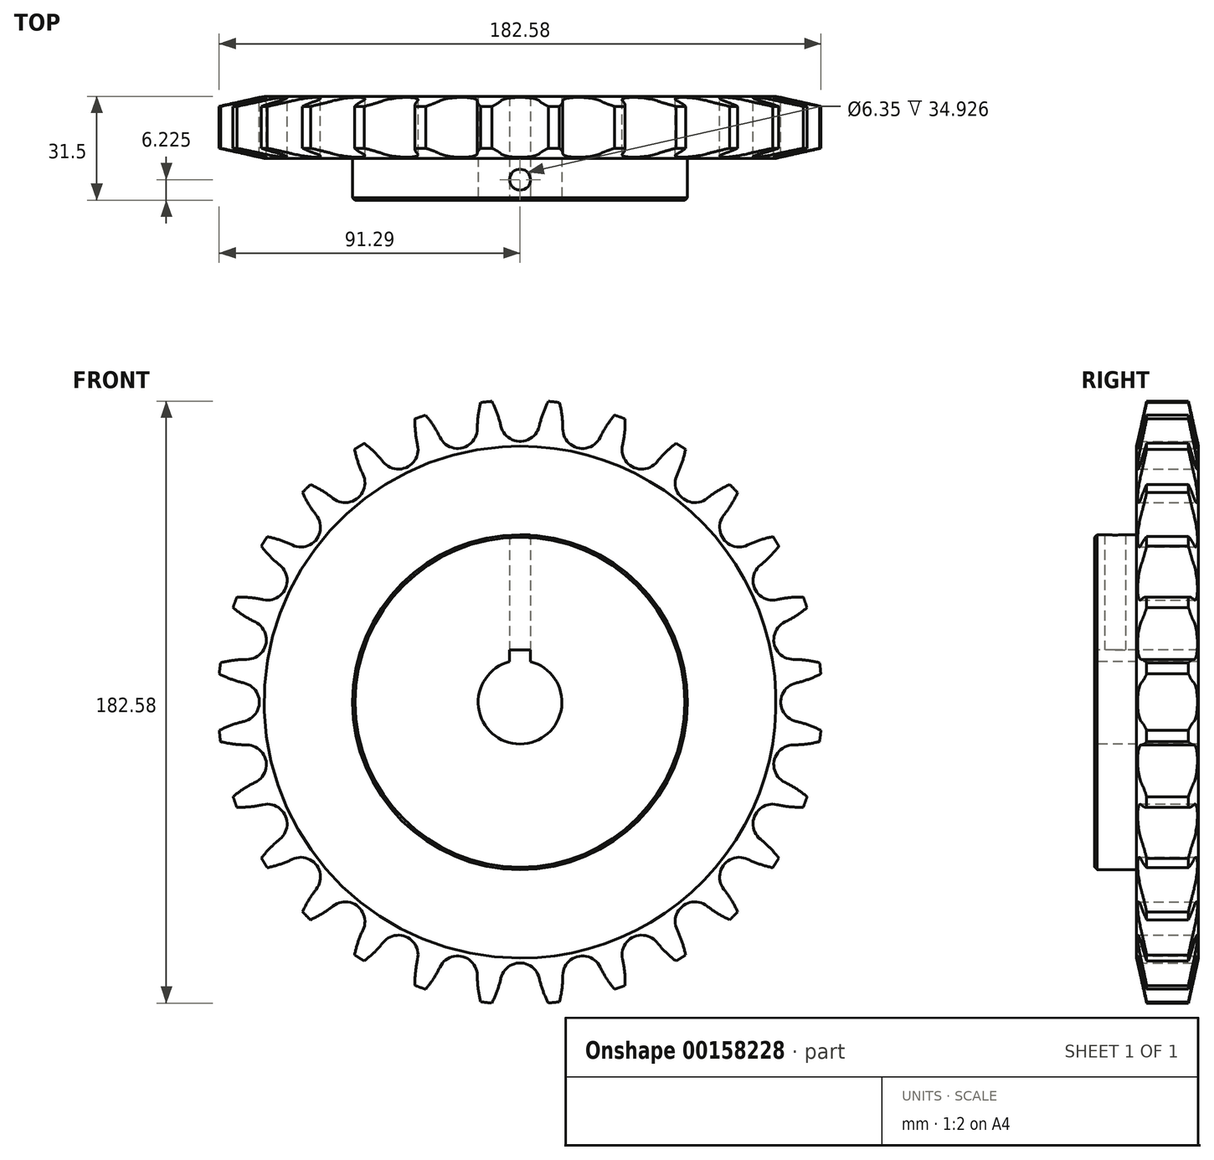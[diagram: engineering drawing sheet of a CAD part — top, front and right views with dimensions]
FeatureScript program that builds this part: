
annotation { "Feature Type Name" : "Feature", "Feature Type Description" : "" }
export const myFeature = defineFeature(function(context is Context, id is Id, definition is map)
    precondition{}
    {
        {
            var Q0;
            Q0=qCreatedBy(makeId("Front.planeOp"),FACE);
            var sketch = newSketch(context, id + "F0", { "sketchPlane" : qUnion([Q0])});
            skCircle(sketch, "E0", {"center": v(0, 0) * mm, "radius": 85.08 * mm, "construction": true});
            skArc(sketch, "E1", {"start": v(11.96, 90.87) * mm, "mid": v(10.27, 91.1) * mm, "end": v(8.58, 91.29) * mm});
            skArc(sketch, "E2", {"start": v(0, 79.1) * mm, "mid": v(3.72, 80.41) * mm, "end": v(5.82, 83.75) * mm});
            skArc(sketch, "E3", {"start": v(12.96, 82.94) * mm, "mid": v(14.26, 79.22) * mm, "end": v(17.6, 77.12) * mm});
            skArc(sketch, "E4", {"start": v(8.58, 91.29) * mm, "mid": v(6.96, 87.6) * mm, "end": v(5.82, 83.75) * mm});
            skArc(sketch, "E5.trimOffspring", {"start": v(12.96, 82.94) * mm, "mid": v(12.71, 86.94) * mm, "end": v(11.96, 90.87) * mm});
            skPoint(sketch, "E6.orphan", {"position": v(0, 104.4) * mm});
            skPoint(sketch, "E7.orphan", {"position": v(23.23, 101.77) * mm});
            skArc(sketch, "E8.1.1", {"start": v(-17.6, 77.12) * mm, "mid": v(-14.26, 79.22) * mm, "end": v(-12.96, 82.94) * mm});
            skArc(sketch, "E8.1.2", {"start": v(-11.95, 90.9) * mm, "mid": v(-12.7, 86.96) * mm, "end": v(-12.96, 82.94) * mm});
            skArc(sketch, "E8.1.3", {"start": v(-8.56, 91.26) * mm, "mid": v(-10.26, 91.1) * mm, "end": v(-11.95, 90.9) * mm});
            skArc(sketch, "E8.1.4", {"start": v(-5.82, 83.75) * mm, "mid": v(-6.95, 87.59) * mm, "end": v(-8.56, 91.26) * mm});
            skArc(sketch, "E8.1.5", {"start": v(-5.82, 83.75) * mm, "mid": v(-3.72, 80.41) * mm, "end": v(0, 79.1) * mm});
            skArc(sketch, "E8.2.1", {"start": v(-34.32, 71.27) * mm, "mid": v(-31.54, 74.06) * mm, "end": v(-31.1, 77.98) * mm});
            skArc(sketch, "E8.2.2", {"start": v(-31.88, 85.97) * mm, "mid": v(-31.74, 81.95) * mm, "end": v(-31.1, 77.98) * mm});
            skArc(sketch, "E8.2.3", {"start": v(-28.65, 87.06) * mm, "mid": v(-30.27, 86.53) * mm, "end": v(-31.88, 85.97) * mm});
            skArc(sketch, "E8.2.4", {"start": v(-24.3, 80.35) * mm, "mid": v(-26.27, 83.84) * mm, "end": v(-28.65, 87.06) * mm});
            skArc(sketch, "E8.2.5", {"start": v(-24.3, 80.35) * mm, "mid": v(-21.52, 77.57) * mm, "end": v(-17.6, 77.12) * mm});
            skArc(sketch, "E8.3.1", {"start": v(-49.32, 61.85) * mm, "mid": v(-47.23, 65.19) * mm, "end": v(-47.67, 69.1) * mm});
            skArc(sketch, "E8.3.2", {"start": v(-50.21, 76.72) * mm, "mid": v(-49.18, 72.83) * mm, "end": v(-47.67, 69.1) * mm});
            skArc(sketch, "E8.3.3", {"start": v(-47.3, 78.5) * mm, "mid": v(-48.77, 77.62) * mm, "end": v(-50.21, 76.72) * mm});
            skArc(sketch, "E8.3.4", {"start": v(-41.58, 72.93) * mm, "mid": v(-44.27, 75.9) * mm, "end": v(-47.3, 78.5) * mm});
            skArc(sketch, "E8.3.5", {"start": v(-41.58, 72.93) * mm, "mid": v(-38.24, 70.83) * mm, "end": v(-34.32, 71.27) * mm});
            skArc(sketch, "E8.4.1", {"start": v(-61.85, 49.32) * mm, "mid": v(-60.55, 53.04) * mm, "end": v(-61.85, 56.77) * mm});
            skArc(sketch, "E8.4.2", {"start": v(-66.02, 63.62) * mm, "mid": v(-64.15, 60.06) * mm, "end": v(-61.85, 56.77) * mm});
            skArc(sketch, "E8.4.3", {"start": v(-63.59, 66) * mm, "mid": v(-64.82, 64.83) * mm, "end": v(-66.02, 63.62) * mm});
            skArc(sketch, "E8.4.4", {"start": v(-56.77, 61.85) * mm, "mid": v(-60.05, 64.14) * mm, "end": v(-63.59, 66) * mm});
            skArc(sketch, "E8.4.5", {"start": v(-56.77, 61.85) * mm, "mid": v(-53.04, 60.55) * mm, "end": v(-49.32, 61.85) * mm});
            skArc(sketch, "E8.5.1", {"start": v(-71.27, 34.32) * mm, "mid": v(-70.83, 38.24) * mm, "end": v(-72.93, 41.58) * mm});
            skArc(sketch, "E8.5.2", {"start": v(-78.53, 47.33) * mm, "mid": v(-75.9, 44.28) * mm, "end": v(-72.93, 41.58) * mm});
            skArc(sketch, "E8.5.3", {"start": v(-76.68, 50.2) * mm, "mid": v(-77.62, 48.78) * mm, "end": v(-78.53, 47.33) * mm});
            skArc(sketch, "E8.5.4", {"start": v(-69.1, 47.67) * mm, "mid": v(-72.81, 49.17) * mm, "end": v(-76.68, 50.2) * mm});
            skArc(sketch, "E8.5.5", {"start": v(-69.1, 47.67) * mm, "mid": v(-65.19, 47.23) * mm, "end": v(-61.85, 49.32) * mm});
            skArc(sketch, "E8.6.1", {"start": v(-77.12, 17.6) * mm, "mid": v(-77.57, 21.52) * mm, "end": v(-80.35, 24.3) * mm});
            skArc(sketch, "E8.6.2", {"start": v(-87.09, 28.67) * mm, "mid": v(-83.86, 26.28) * mm, "end": v(-80.35, 24.3) * mm});
            skArc(sketch, "E8.6.3", {"start": v(-85.93, 31.88) * mm, "mid": v(-86.53, 30.28) * mm, "end": v(-87.09, 28.67) * mm});
            skArc(sketch, "E8.6.4", {"start": v(-77.98, 31.1) * mm, "mid": v(-81.93, 31.74) * mm, "end": v(-85.93, 31.88) * mm});
            skArc(sketch, "E8.6.5", {"start": v(-77.98, 31.1) * mm, "mid": v(-74.06, 31.54) * mm, "end": v(-71.27, 34.32) * mm});
            skArc(sketch, "E8.7.1", {"start": v(-79.1, 0) * mm, "mid": v(-80.41, 3.72) * mm, "end": v(-83.75, 5.82) * mm});
            skArc(sketch, "E8.7.2", {"start": v(-91.29, 8.58) * mm, "mid": v(-87.6, 6.96) * mm, "end": v(-83.75, 5.82) * mm});
            skArc(sketch, "E8.7.3", {"start": v(-90.87, 11.96) * mm, "mid": v(-91.1, 10.27) * mm, "end": v(-91.29, 8.58) * mm});
            skArc(sketch, "E8.7.4", {"start": v(-82.94, 12.96) * mm, "mid": v(-86.94, 12.71) * mm, "end": v(-90.87, 11.96) * mm});
            skArc(sketch, "E8.7.5", {"start": v(-82.94, 12.96) * mm, "mid": v(-79.22, 14.26) * mm, "end": v(-77.12, 17.6) * mm});
            skArc(sketch, "E8.8.1", {"start": v(-77.12, -17.6) * mm, "mid": v(-79.22, -14.26) * mm, "end": v(-82.94, -12.96) * mm});
            skArc(sketch, "E8.8.2", {"start": v(-90.9, -11.95) * mm, "mid": v(-86.96, -12.7) * mm, "end": v(-82.94, -12.96) * mm});
            skArc(sketch, "E8.8.3", {"start": v(-91.26, -8.56) * mm, "mid": v(-91.1, -10.26) * mm, "end": v(-90.9, -11.95) * mm});
            skArc(sketch, "E8.8.4", {"start": v(-83.75, -5.82) * mm, "mid": v(-87.59, -6.95) * mm, "end": v(-91.26, -8.56) * mm});
            skArc(sketch, "E8.8.5", {"start": v(-83.75, -5.82) * mm, "mid": v(-80.41, -3.72) * mm, "end": v(-79.1, 0) * mm});
            skArc(sketch, "E8.9.1", {"start": v(-71.27, -34.32) * mm, "mid": v(-74.06, -31.54) * mm, "end": v(-77.98, -31.1) * mm});
            skArc(sketch, "E8.9.2", {"start": v(-85.97, -31.88) * mm, "mid": v(-81.95, -31.74) * mm, "end": v(-77.98, -31.1) * mm});
            skArc(sketch, "E8.9.3", {"start": v(-87.06, -28.65) * mm, "mid": v(-86.53, -30.27) * mm, "end": v(-85.97, -31.88) * mm});
            skArc(sketch, "E8.9.4", {"start": v(-80.35, -24.3) * mm, "mid": v(-83.84, -26.27) * mm, "end": v(-87.06, -28.65) * mm});
            skArc(sketch, "E8.9.5", {"start": v(-80.35, -24.3) * mm, "mid": v(-77.57, -21.52) * mm, "end": v(-77.12, -17.6) * mm});
            skArc(sketch, "E8.10.1", {"start": v(-61.85, -49.32) * mm, "mid": v(-65.19, -47.23) * mm, "end": v(-69.1, -47.67) * mm});
            skArc(sketch, "E8.10.2", {"start": v(-76.72, -50.21) * mm, "mid": v(-72.83, -49.18) * mm, "end": v(-69.1, -47.67) * mm});
            skArc(sketch, "E8.10.3", {"start": v(-78.5, -47.3) * mm, "mid": v(-77.62, -48.77) * mm, "end": v(-76.72, -50.21) * mm});
            skArc(sketch, "E8.10.4", {"start": v(-72.93, -41.58) * mm, "mid": v(-75.9, -44.27) * mm, "end": v(-78.5, -47.3) * mm});
            skArc(sketch, "E8.10.5", {"start": v(-72.93, -41.58) * mm, "mid": v(-70.83, -38.24) * mm, "end": v(-71.27, -34.32) * mm});
            skArc(sketch, "E8.11.1", {"start": v(-49.32, -61.85) * mm, "mid": v(-53.04, -60.55) * mm, "end": v(-56.77, -61.85) * mm});
            skArc(sketch, "E8.11.2", {"start": v(-63.62, -66.02) * mm, "mid": v(-60.06, -64.15) * mm, "end": v(-56.77, -61.85) * mm});
            skArc(sketch, "E8.11.3", {"start": v(-66, -63.59) * mm, "mid": v(-64.83, -64.82) * mm, "end": v(-63.62, -66.02) * mm});
            skArc(sketch, "E8.11.4", {"start": v(-61.85, -56.77) * mm, "mid": v(-64.14, -60.05) * mm, "end": v(-66, -63.59) * mm});
            skArc(sketch, "E8.11.5", {"start": v(-61.85, -56.77) * mm, "mid": v(-60.55, -53.04) * mm, "end": v(-61.85, -49.32) * mm});
            skArc(sketch, "E8.12.1", {"start": v(-34.32, -71.27) * mm, "mid": v(-38.24, -70.83) * mm, "end": v(-41.58, -72.93) * mm});
            skArc(sketch, "E8.12.2", {"start": v(-47.33, -78.53) * mm, "mid": v(-44.28, -75.9) * mm, "end": v(-41.58, -72.93) * mm});
            skArc(sketch, "E8.12.3", {"start": v(-50.2, -76.68) * mm, "mid": v(-48.78, -77.62) * mm, "end": v(-47.33, -78.53) * mm});
            skArc(sketch, "E8.12.4", {"start": v(-47.67, -69.1) * mm, "mid": v(-49.17, -72.81) * mm, "end": v(-50.2, -76.68) * mm});
            skArc(sketch, "E8.12.5", {"start": v(-47.67, -69.1) * mm, "mid": v(-47.23, -65.19) * mm, "end": v(-49.32, -61.85) * mm});
            skArc(sketch, "E8.13.1", {"start": v(-17.6, -77.12) * mm, "mid": v(-21.52, -77.57) * mm, "end": v(-24.3, -80.35) * mm});
            skArc(sketch, "E8.13.2", {"start": v(-28.67, -87.09) * mm, "mid": v(-26.28, -83.86) * mm, "end": v(-24.3, -80.35) * mm});
            skArc(sketch, "E8.13.3", {"start": v(-31.88, -85.93) * mm, "mid": v(-30.28, -86.53) * mm, "end": v(-28.67, -87.09) * mm});
            skArc(sketch, "E8.13.4", {"start": v(-31.1, -77.98) * mm, "mid": v(-31.74, -81.93) * mm, "end": v(-31.88, -85.93) * mm});
            skArc(sketch, "E8.13.5", {"start": v(-31.1, -77.98) * mm, "mid": v(-31.54, -74.06) * mm, "end": v(-34.32, -71.27) * mm});
            skArc(sketch, "E8.14.1", {"start": v(0, -79.1) * mm, "mid": v(-3.72, -80.41) * mm, "end": v(-5.82, -83.75) * mm});
            skArc(sketch, "E8.14.2", {"start": v(-8.58, -91.29) * mm, "mid": v(-6.96, -87.6) * mm, "end": v(-5.82, -83.75) * mm});
            skArc(sketch, "E8.14.3", {"start": v(-11.96, -90.87) * mm, "mid": v(-10.27, -91.1) * mm, "end": v(-8.58, -91.29) * mm});
            skArc(sketch, "E8.14.4", {"start": v(-12.96, -82.94) * mm, "mid": v(-12.71, -86.94) * mm, "end": v(-11.96, -90.87) * mm});
            skArc(sketch, "E8.14.5", {"start": v(-12.96, -82.94) * mm, "mid": v(-14.26, -79.22) * mm, "end": v(-17.6, -77.12) * mm});
            skArc(sketch, "E8.15.1", {"start": v(17.6, -77.12) * mm, "mid": v(14.26, -79.22) * mm, "end": v(12.96, -82.94) * mm});
            skArc(sketch, "E8.15.2", {"start": v(11.95, -90.9) * mm, "mid": v(12.7, -86.96) * mm, "end": v(12.96, -82.94) * mm});
            skArc(sketch, "E8.15.3", {"start": v(8.56, -91.26) * mm, "mid": v(10.26, -91.1) * mm, "end": v(11.95, -90.9) * mm});
            skArc(sketch, "E8.15.4", {"start": v(5.82, -83.75) * mm, "mid": v(6.95, -87.59) * mm, "end": v(8.56, -91.26) * mm});
            skArc(sketch, "E8.15.5", {"start": v(5.82, -83.75) * mm, "mid": v(3.72, -80.41) * mm, "end": v(0, -79.1) * mm});
            skArc(sketch, "E8.16.1", {"start": v(34.32, -71.27) * mm, "mid": v(31.54, -74.06) * mm, "end": v(31.1, -77.98) * mm});
            skArc(sketch, "E8.16.2", {"start": v(31.88, -85.97) * mm, "mid": v(31.74, -81.95) * mm, "end": v(31.1, -77.98) * mm});
            skArc(sketch, "E8.16.3", {"start": v(28.65, -87.06) * mm, "mid": v(30.27, -86.53) * mm, "end": v(31.88, -85.97) * mm});
            skArc(sketch, "E8.16.4", {"start": v(24.3, -80.35) * mm, "mid": v(26.27, -83.84) * mm, "end": v(28.65, -87.06) * mm});
            skArc(sketch, "E8.16.5", {"start": v(24.3, -80.35) * mm, "mid": v(21.52, -77.57) * mm, "end": v(17.6, -77.12) * mm});
            skArc(sketch, "E8.17.1", {"start": v(49.32, -61.85) * mm, "mid": v(47.23, -65.19) * mm, "end": v(47.67, -69.1) * mm});
            skArc(sketch, "E8.17.2", {"start": v(50.21, -76.72) * mm, "mid": v(49.18, -72.83) * mm, "end": v(47.67, -69.1) * mm});
            skArc(sketch, "E8.17.3", {"start": v(47.3, -78.5) * mm, "mid": v(48.77, -77.62) * mm, "end": v(50.21, -76.72) * mm});
            skArc(sketch, "E8.17.4", {"start": v(41.58, -72.93) * mm, "mid": v(44.27, -75.9) * mm, "end": v(47.3, -78.5) * mm});
            skArc(sketch, "E8.17.5", {"start": v(41.58, -72.93) * mm, "mid": v(38.24, -70.83) * mm, "end": v(34.32, -71.27) * mm});
            skArc(sketch, "E8.18.1", {"start": v(61.85, -49.32) * mm, "mid": v(60.55, -53.04) * mm, "end": v(61.85, -56.77) * mm});
            skArc(sketch, "E8.18.2", {"start": v(66.02, -63.62) * mm, "mid": v(64.15, -60.06) * mm, "end": v(61.85, -56.77) * mm});
            skArc(sketch, "E8.18.3", {"start": v(63.59, -66) * mm, "mid": v(64.82, -64.83) * mm, "end": v(66.02, -63.62) * mm});
            skArc(sketch, "E8.18.4", {"start": v(56.77, -61.85) * mm, "mid": v(60.05, -64.14) * mm, "end": v(63.59, -66) * mm});
            skArc(sketch, "E8.18.5", {"start": v(56.77, -61.85) * mm, "mid": v(53.04, -60.55) * mm, "end": v(49.32, -61.85) * mm});
            skArc(sketch, "E8.19.1", {"start": v(71.27, -34.32) * mm, "mid": v(70.83, -38.24) * mm, "end": v(72.93, -41.58) * mm});
            skArc(sketch, "E8.19.2", {"start": v(78.53, -47.33) * mm, "mid": v(75.9, -44.28) * mm, "end": v(72.93, -41.58) * mm});
            skArc(sketch, "E8.19.3", {"start": v(76.68, -50.2) * mm, "mid": v(77.62, -48.78) * mm, "end": v(78.53, -47.33) * mm});
            skArc(sketch, "E8.19.4", {"start": v(69.1, -47.67) * mm, "mid": v(72.81, -49.17) * mm, "end": v(76.68, -50.2) * mm});
            skArc(sketch, "E8.19.5", {"start": v(69.1, -47.67) * mm, "mid": v(65.19, -47.23) * mm, "end": v(61.85, -49.32) * mm});
            skArc(sketch, "E8.20.1", {"start": v(77.12, -17.6) * mm, "mid": v(77.57, -21.52) * mm, "end": v(80.35, -24.3) * mm});
            skArc(sketch, "E8.20.2", {"start": v(87.09, -28.67) * mm, "mid": v(83.86, -26.28) * mm, "end": v(80.35, -24.3) * mm});
            skArc(sketch, "E8.20.3", {"start": v(85.93, -31.88) * mm, "mid": v(86.53, -30.28) * mm, "end": v(87.09, -28.67) * mm});
            skArc(sketch, "E8.20.4", {"start": v(77.98, -31.1) * mm, "mid": v(81.93, -31.74) * mm, "end": v(85.93, -31.88) * mm});
            skArc(sketch, "E8.20.5", {"start": v(77.98, -31.1) * mm, "mid": v(74.06, -31.54) * mm, "end": v(71.27, -34.32) * mm});
            skArc(sketch, "E8.21.1", {"start": v(79.1, 0) * mm, "mid": v(80.41, -3.72) * mm, "end": v(83.75, -5.82) * mm});
            skArc(sketch, "E8.21.2", {"start": v(91.29, -8.58) * mm, "mid": v(87.6, -6.96) * mm, "end": v(83.75, -5.82) * mm});
            skArc(sketch, "E8.21.3", {"start": v(90.87, -11.96) * mm, "mid": v(91.1, -10.27) * mm, "end": v(91.29, -8.58) * mm});
            skArc(sketch, "E8.21.4", {"start": v(82.94, -12.96) * mm, "mid": v(86.94, -12.71) * mm, "end": v(90.87, -11.96) * mm});
            skArc(sketch, "E8.21.5", {"start": v(82.94, -12.96) * mm, "mid": v(79.22, -14.26) * mm, "end": v(77.12, -17.6) * mm});
            skArc(sketch, "E8.22.1", {"start": v(77.12, 17.6) * mm, "mid": v(79.22, 14.26) * mm, "end": v(82.94, 12.96) * mm});
            skArc(sketch, "E8.22.2", {"start": v(90.9, 11.95) * mm, "mid": v(86.96, 12.7) * mm, "end": v(82.94, 12.96) * mm});
            skArc(sketch, "E8.22.3", {"start": v(91.26, 8.56) * mm, "mid": v(91.1, 10.26) * mm, "end": v(90.9, 11.95) * mm});
            skArc(sketch, "E8.22.4", {"start": v(83.75, 5.82) * mm, "mid": v(87.59, 6.95) * mm, "end": v(91.26, 8.56) * mm});
            skArc(sketch, "E8.22.5", {"start": v(83.75, 5.82) * mm, "mid": v(80.41, 3.72) * mm, "end": v(79.1, 0) * mm});
            skArc(sketch, "E8.23.1", {"start": v(71.27, 34.32) * mm, "mid": v(74.06, 31.54) * mm, "end": v(77.98, 31.1) * mm});
            skArc(sketch, "E8.23.2", {"start": v(85.97, 31.88) * mm, "mid": v(81.95, 31.74) * mm, "end": v(77.98, 31.1) * mm});
            skArc(sketch, "E8.23.3", {"start": v(87.06, 28.65) * mm, "mid": v(86.53, 30.27) * mm, "end": v(85.97, 31.88) * mm});
            skArc(sketch, "E8.23.4", {"start": v(80.35, 24.3) * mm, "mid": v(83.84, 26.27) * mm, "end": v(87.06, 28.65) * mm});
            skArc(sketch, "E8.23.5", {"start": v(80.35, 24.3) * mm, "mid": v(77.57, 21.52) * mm, "end": v(77.12, 17.6) * mm});
            skArc(sketch, "E8.24.1", {"start": v(61.85, 49.32) * mm, "mid": v(65.19, 47.23) * mm, "end": v(69.1, 47.67) * mm});
            skArc(sketch, "E8.24.2", {"start": v(76.72, 50.21) * mm, "mid": v(72.83, 49.18) * mm, "end": v(69.1, 47.67) * mm});
            skArc(sketch, "E8.24.3", {"start": v(78.5, 47.3) * mm, "mid": v(77.62, 48.77) * mm, "end": v(76.72, 50.21) * mm});
            skArc(sketch, "E8.24.4", {"start": v(72.93, 41.58) * mm, "mid": v(75.9, 44.27) * mm, "end": v(78.5, 47.3) * mm});
            skArc(sketch, "E8.24.5", {"start": v(72.93, 41.58) * mm, "mid": v(70.83, 38.24) * mm, "end": v(71.27, 34.32) * mm});
            skArc(sketch, "E8.25.1", {"start": v(49.32, 61.85) * mm, "mid": v(53.04, 60.55) * mm, "end": v(56.77, 61.85) * mm});
            skArc(sketch, "E8.25.2", {"start": v(63.62, 66.02) * mm, "mid": v(60.06, 64.15) * mm, "end": v(56.77, 61.85) * mm});
            skArc(sketch, "E8.25.3", {"start": v(66, 63.59) * mm, "mid": v(64.83, 64.82) * mm, "end": v(63.62, 66.02) * mm});
            skArc(sketch, "E8.25.4", {"start": v(61.85, 56.77) * mm, "mid": v(64.14, 60.05) * mm, "end": v(66, 63.59) * mm});
            skArc(sketch, "E8.25.5", {"start": v(61.85, 56.77) * mm, "mid": v(60.55, 53.04) * mm, "end": v(61.85, 49.32) * mm});
            skArc(sketch, "E8.26.1", {"start": v(34.32, 71.27) * mm, "mid": v(38.24, 70.83) * mm, "end": v(41.58, 72.93) * mm});
            skArc(sketch, "E8.26.2", {"start": v(47.33, 78.53) * mm, "mid": v(44.28, 75.9) * mm, "end": v(41.58, 72.93) * mm});
            skArc(sketch, "E8.26.3", {"start": v(50.2, 76.68) * mm, "mid": v(48.78, 77.62) * mm, "end": v(47.33, 78.53) * mm});
            skArc(sketch, "E8.26.4", {"start": v(47.67, 69.1) * mm, "mid": v(49.17, 72.81) * mm, "end": v(50.2, 76.68) * mm});
            skArc(sketch, "E8.26.5", {"start": v(47.67, 69.1) * mm, "mid": v(47.23, 65.19) * mm, "end": v(49.32, 61.85) * mm});
            skArc(sketch, "E8.27.1", {"start": v(17.6, 77.12) * mm, "mid": v(21.52, 77.57) * mm, "end": v(24.3, 80.35) * mm});
            skArc(sketch, "E8.27.2", {"start": v(28.67, 87.09) * mm, "mid": v(26.28, 83.86) * mm, "end": v(24.3, 80.35) * mm});
            skArc(sketch, "E8.27.3", {"start": v(31.88, 85.93) * mm, "mid": v(30.28, 86.53) * mm, "end": v(28.67, 87.09) * mm});
            skArc(sketch, "E8.27.4", {"start": v(31.1, 77.98) * mm, "mid": v(31.74, 81.93) * mm, "end": v(31.88, 85.93) * mm});
            skArc(sketch, "E8.27.5", {"start": v(31.1, 77.98) * mm, "mid": v(31.54, 74.06) * mm, "end": v(34.32, 71.27) * mm});
            skSolve(sketch);
        }
        {
            var Q0;
            Q0=makeQuery(id+"F0.imprint","IMPRINT",FACE,{"disambiguationData":[TD([[makeQuery(id+"F0.imprint","IMPRINT",EDGE,{"derivedFrom":sQuery(id+"F0.wireOp",EDGE,"E1")}),1.0]])]});
            extrude(context, id + "F1", {"entities" : qUnion([Q0]), "endBound" : BoundingType.SYMMETRIC, "depth" : 18.8 * mm});
        }
        {
            var Q0;
            Q0=qCreatedBy(makeId("Right.planeOp"),FACE);
            var sketch = newSketch(context, id + "F2", { "sketchPlane" : qUnion([Q0])});
            skLineSegment(sketch, "E9", {"start": v(-5.4, 96) * mm, "end": v(-10.8, 71.24) * mm});
            skLineSegment(sketch, "E10", {"start": v(-10.8, 71.24) * mm, "end": v(-10.8, 96) * mm});
            skLineSegment(sketch, "E11", {"start": v(-10.8, 96) * mm, "end": v(-5.4, 96) * mm});
            skLineSegment(sketch, "E12.MirrorCS", {"start": v(10.8, 96) * mm, "end": v(5.4, 96) * mm});
            skLineSegment(sketch, "E13.MirrorCS", {"start": v(10.8, 71.24) * mm, "end": v(10.8, 96) * mm});
            skLineSegment(sketch, "E14.MirrorCS", {"start": v(5.4, 96) * mm, "end": v(10.8, 71.24) * mm});
            skSolve(sketch);
        }
        {
            var Q0;
            Q0=qCreatedBy(makeId("Top.planeOp"),FACE);
            var sketch = newSketch(context, id + "F3", { "sketchPlane" : qUnion([Q0])});
            skLineSegment(sketch, "E15", {"start": v(0, -2) * mm, "end": v(0, -80.69) * mm, "construction": true});
            skSolve(sketch);
        }
        {
            var Q0;
            Q0=makeQuery(id+"F2.imprint","IMPRINT",FACE,{"disambiguationData":[TD([[makeQuery(id+"F2.imprint","IMPRINT",EDGE,{"derivedFrom":sQuery(id+"F2.wireOp",EDGE,"E9")}),-1.0]])]});
            var Q1;
            Q1=makeQuery(id+"F2.imprint","IMPRINT",FACE,{"disambiguationData":[TD([[makeQuery(id+"F2.imprint","IMPRINT",EDGE,{"derivedFrom":sQuery(id+"F2.wireOp",EDGE,"E12.MirrorCS")}),1.0]])]});
            var Q2;
            Q2=sQuery(id+"F3.wireOp",EDGE,"E15");
            revolve(context, id + "F4", {"operationType" : NewBodyOperationType.REMOVE, "entities" : qUnion([Q0, Q1]), "axis" : qUnion([Q2]), "revolveType" : RevolveType.FULL, "oppositeDirection" : true});
        }
        {
            var Q0;
            Q0=makeQuery(id+"F1.opExtrude","CAP_FACE",FACE,{"disambiguationData":[OSD([sQuery(id+"F0.wireOp",EDGE,"E1"),sQuery(id+"F0.wireOp",EDGE,"E2"),sQuery(id+"F0.wireOp",EDGE,"E3"),sQuery(id+"F0.wireOp",EDGE,"E4"),sQuery(id+"F0.wireOp",EDGE,"E5.trimOffspring"),sQuery(id+"F0.wireOp",EDGE,"E8.1.1"),sQuery(id+"F0.wireOp",EDGE,"E8.1.2"),sQuery(id+"F0.wireOp",EDGE,"E8.1.3"),sQuery(id+"F0.wireOp",EDGE,"E8.1.4"),sQuery(id+"F0.wireOp",EDGE,"E8.1.5"),sQuery(id+"F0.wireOp",EDGE,"E8.2.1"),sQuery(id+"F0.wireOp",EDGE,"E8.2.2"),sQuery(id+"F0.wireOp",EDGE,"E8.2.3"),sQuery(id+"F0.wireOp",EDGE,"E8.2.4"),sQuery(id+"F0.wireOp",EDGE,"E8.2.5"),sQuery(id+"F0.wireOp",EDGE,"E8.3.1"),sQuery(id+"F0.wireOp",EDGE,"E8.3.2"),sQuery(id+"F0.wireOp",EDGE,"E8.3.3"),sQuery(id+"F0.wireOp",EDGE,"E8.3.4"),sQuery(id+"F0.wireOp",EDGE,"E8.3.5"),sQuery(id+"F0.wireOp",EDGE,"E8.4.1"),sQuery(id+"F0.wireOp",EDGE,"E8.4.2"),sQuery(id+"F0.wireOp",EDGE,"E8.4.3"),sQuery(id+"F0.wireOp",EDGE,"E8.4.4"),sQuery(id+"F0.wireOp",EDGE,"E8.4.5"),sQuery(id+"F0.wireOp",EDGE,"E8.5.1"),sQuery(id+"F0.wireOp",EDGE,"E8.5.2"),sQuery(id+"F0.wireOp",EDGE,"E8.5.3"),sQuery(id+"F0.wireOp",EDGE,"E8.5.4"),sQuery(id+"F0.wireOp",EDGE,"E8.5.5"),sQuery(id+"F0.wireOp",EDGE,"E8.6.1"),sQuery(id+"F0.wireOp",EDGE,"E8.6.2"),sQuery(id+"F0.wireOp",EDGE,"E8.6.3"),sQuery(id+"F0.wireOp",EDGE,"E8.6.4"),sQuery(id+"F0.wireOp",EDGE,"E8.6.5"),sQuery(id+"F0.wireOp",EDGE,"E8.7.1"),sQuery(id+"F0.wireOp",EDGE,"E8.7.2"),sQuery(id+"F0.wireOp",EDGE,"E8.7.3"),sQuery(id+"F0.wireOp",EDGE,"E8.7.4"),sQuery(id+"F0.wireOp",EDGE,"E8.7.5"),sQuery(id+"F0.wireOp",EDGE,"E8.8.1"),sQuery(id+"F0.wireOp",EDGE,"E8.8.2"),sQuery(id+"F0.wireOp",EDGE,"E8.8.3"),sQuery(id+"F0.wireOp",EDGE,"E8.8.4"),sQuery(id+"F0.wireOp",EDGE,"E8.8.5"),sQuery(id+"F0.wireOp",EDGE,"E8.9.1"),sQuery(id+"F0.wireOp",EDGE,"E8.9.2"),sQuery(id+"F0.wireOp",EDGE,"E8.9.3"),sQuery(id+"F0.wireOp",EDGE,"E8.9.4"),sQuery(id+"F0.wireOp",EDGE,"E8.9.5"),sQuery(id+"F0.wireOp",EDGE,"E8.10.1"),sQuery(id+"F0.wireOp",EDGE,"E8.10.2"),sQuery(id+"F0.wireOp",EDGE,"E8.10.3"),sQuery(id+"F0.wireOp",EDGE,"E8.10.4"),sQuery(id+"F0.wireOp",EDGE,"E8.10.5"),sQuery(id+"F0.wireOp",EDGE,"E8.11.1"),sQuery(id+"F0.wireOp",EDGE,"E8.11.2"),sQuery(id+"F0.wireOp",EDGE,"E8.11.3"),sQuery(id+"F0.wireOp",EDGE,"E8.11.4"),sQuery(id+"F0.wireOp",EDGE,"E8.11.5"),sQuery(id+"F0.wireOp",EDGE,"E8.12.1"),sQuery(id+"F0.wireOp",EDGE,"E8.12.2"),sQuery(id+"F0.wireOp",EDGE,"E8.12.3"),sQuery(id+"F0.wireOp",EDGE,"E8.12.4"),sQuery(id+"F0.wireOp",EDGE,"E8.12.5"),sQuery(id+"F0.wireOp",EDGE,"E8.13.1"),sQuery(id+"F0.wireOp",EDGE,"E8.13.2"),sQuery(id+"F0.wireOp",EDGE,"E8.13.3"),sQuery(id+"F0.wireOp",EDGE,"E8.13.4"),sQuery(id+"F0.wireOp",EDGE,"E8.13.5"),sQuery(id+"F0.wireOp",EDGE,"E8.14.1"),sQuery(id+"F0.wireOp",EDGE,"E8.14.2"),sQuery(id+"F0.wireOp",EDGE,"E8.14.3"),sQuery(id+"F0.wireOp",EDGE,"E8.14.4"),sQuery(id+"F0.wireOp",EDGE,"E8.14.5"),sQuery(id+"F0.wireOp",EDGE,"E8.15.1"),sQuery(id+"F0.wireOp",EDGE,"E8.15.2"),sQuery(id+"F0.wireOp",EDGE,"E8.15.3"),sQuery(id+"F0.wireOp",EDGE,"E8.15.4"),sQuery(id+"F0.wireOp",EDGE,"E8.15.5"),sQuery(id+"F0.wireOp",EDGE,"E8.16.1"),sQuery(id+"F0.wireOp",EDGE,"E8.16.2"),sQuery(id+"F0.wireOp",EDGE,"E8.16.3"),sQuery(id+"F0.wireOp",EDGE,"E8.16.4"),sQuery(id+"F0.wireOp",EDGE,"E8.16.5"),sQuery(id+"F0.wireOp",EDGE,"E8.17.1"),sQuery(id+"F0.wireOp",EDGE,"E8.17.2"),sQuery(id+"F0.wireOp",EDGE,"E8.17.3"),sQuery(id+"F0.wireOp",EDGE,"E8.17.4"),sQuery(id+"F0.wireOp",EDGE,"E8.17.5"),sQuery(id+"F0.wireOp",EDGE,"E8.18.1"),sQuery(id+"F0.wireOp",EDGE,"E8.18.2"),sQuery(id+"F0.wireOp",EDGE,"E8.18.3"),sQuery(id+"F0.wireOp",EDGE,"E8.18.4"),sQuery(id+"F0.wireOp",EDGE,"E8.18.5"),sQuery(id+"F0.wireOp",EDGE,"E8.19.1"),sQuery(id+"F0.wireOp",EDGE,"E8.19.2"),sQuery(id+"F0.wireOp",EDGE,"E8.19.3"),sQuery(id+"F0.wireOp",EDGE,"E8.19.4"),sQuery(id+"F0.wireOp",EDGE,"E8.19.5"),sQuery(id+"F0.wireOp",EDGE,"E8.20.1"),sQuery(id+"F0.wireOp",EDGE,"E8.20.2"),sQuery(id+"F0.wireOp",EDGE,"E8.20.3"),sQuery(id+"F0.wireOp",EDGE,"E8.20.4"),sQuery(id+"F0.wireOp",EDGE,"E8.20.5"),sQuery(id+"F0.wireOp",EDGE,"E8.21.1"),sQuery(id+"F0.wireOp",EDGE,"E8.21.2"),sQuery(id+"F0.wireOp",EDGE,"E8.21.3"),sQuery(id+"F0.wireOp",EDGE,"E8.21.4"),sQuery(id+"F0.wireOp",EDGE,"E8.21.5"),sQuery(id+"F0.wireOp",EDGE,"E8.22.1"),sQuery(id+"F0.wireOp",EDGE,"E8.22.2"),sQuery(id+"F0.wireOp",EDGE,"E8.22.3"),sQuery(id+"F0.wireOp",EDGE,"E8.22.4"),sQuery(id+"F0.wireOp",EDGE,"E8.22.5"),sQuery(id+"F0.wireOp",EDGE,"E8.23.1"),sQuery(id+"F0.wireOp",EDGE,"E8.23.2"),sQuery(id+"F0.wireOp",EDGE,"E8.23.3"),sQuery(id+"F0.wireOp",EDGE,"E8.23.4"),sQuery(id+"F0.wireOp",EDGE,"E8.23.5"),sQuery(id+"F0.wireOp",EDGE,"E8.24.1"),sQuery(id+"F0.wireOp",EDGE,"E8.24.2"),sQuery(id+"F0.wireOp",EDGE,"E8.24.3"),sQuery(id+"F0.wireOp",EDGE,"E8.24.4"),sQuery(id+"F0.wireOp",EDGE,"E8.24.5"),sQuery(id+"F0.wireOp",EDGE,"E8.25.1"),sQuery(id+"F0.wireOp",EDGE,"E8.25.2"),sQuery(id+"F0.wireOp",EDGE,"E8.25.3"),sQuery(id+"F0.wireOp",EDGE,"E8.25.4"),sQuery(id+"F0.wireOp",EDGE,"E8.25.5"),sQuery(id+"F0.wireOp",EDGE,"E8.26.1"),sQuery(id+"F0.wireOp",EDGE,"E8.26.2"),sQuery(id+"F0.wireOp",EDGE,"E8.26.3"),sQuery(id+"F0.wireOp",EDGE,"E8.26.4"),sQuery(id+"F0.wireOp",EDGE,"E8.26.5"),sQuery(id+"F0.wireOp",EDGE,"E8.27.1"),sQuery(id+"F0.wireOp",EDGE,"E8.27.2"),sQuery(id+"F0.wireOp",EDGE,"E8.27.3"),sQuery(id+"F0.wireOp",EDGE,"E8.27.4"),sQuery(id+"F0.wireOp",EDGE,"E8.27.5")])],"isStart":false});
            var sketch = newSketch(context, id + "F5", { "sketchPlane" : qUnion([Q0])});
            skCircle(sketch, "E16", {"center": v(0, 0) * mm, "radius": 50.8 * mm});
            skSolve(sketch);
        }
        {
            var Q0;
            Q0=makeQuery(id+"F5.imprint","IMPRINT",FACE,{"disambiguationData":[TD([[makeQuery(id+"F5.imprint","IMPRINT",EDGE,{"derivedFrom":sQuery(id+"F5.wireOp",EDGE,"E16")}),1.0]])]});
            extrude(context, id + "F6", {"entities" : qUnion([Q0]), "operationType" : NewBodyOperationType.ADD, "depth" : 12.7 * mm});
        }
        {
            var Q0;
            Q0=qCreatedBy(makeId("Front.planeOp"),FACE);
            var sketch = newSketch(context, id + "F7", { "sketchPlane" : qUnion([Q0])});
            skArc(sketch, "E17", {"start": v(-3.18, 12.3) * mm, "mid": v(0, -12.7) * mm, "end": v(3.18, 12.3) * mm});
            skLineSegment(sketch, "E18.bottom", {"start": v(3.17, 15.88) * mm, "end": v(-3.18, 15.88) * mm});
            skLineSegment(sketch, "E18.left", {"start": v(3.17, 15.88) * mm, "end": v(3.17, 12.3) * mm});
            skLineSegment(sketch, "E18.right", {"start": v(-3.18, 15.88) * mm, "end": v(-3.18, 12.3) * mm});
            skPoint(sketch, "E18.middle", {"position": v(0, 12.7) * mm});
            skPoint(sketch, "E19.orphan", {"position": v(3.18, 9.53) * mm});
            skPoint(sketch, "E20.orphan", {"position": v(-3.18, 9.53) * mm});
            skSolve(sketch);
        }
        {
            var Q0;
            Q0 = qSketchRegion(id + "F7", true);
            extrude(context, id + "F8", {"entities" : qUnion([Q0]), "operationType" : NewBodyOperationType.REMOVE, "endBound" : BoundingType.SYMMETRIC, "oppositeDirection" : true, "depth" : 101.6 * mm});
        }
        {
            var Q0;
            Q0=makeQuery(id+"F6.opExtrude","CAP_EDGE",EDGE,{"disambiguationData":[OSD([sQuery(id+"F5.wireOp",EDGE,"E16")])],"isStart":false});
            chamfer(context, id + "F9", {"entities" : qUnion([Q0]), "width" : 0.76 * mm, "tangentPropagation" : true});
        }
        {
            var Q0;
            Q0=qCreatedBy(makeId("Top.planeOp"),FACE);
            var sketch = newSketch(context, id + "F10", { "sketchPlane" : qUnion([Q0])});
            skCircle(sketch, "E21", {"center": v(0, -15.88) * mm, "radius": 3.18 * mm});
            skSolve(sketch);
        }
        {
            var Q0;
            Q0=makeQuery(id+"F10.imprint","IMPRINT",FACE,{"disambiguationData":[TD([[makeQuery(id+"F10.imprint","IMPRINT",EDGE,{"derivedFrom":sQuery(id+"F10.wireOp",EDGE,"E21")}),1.0]])]});
            extrude(context, id + "F11", {"entities" : qUnion([Q0]), "operationType" : NewBodyOperationType.REMOVE, "depth" : 101.6 * mm});
        }
    });
